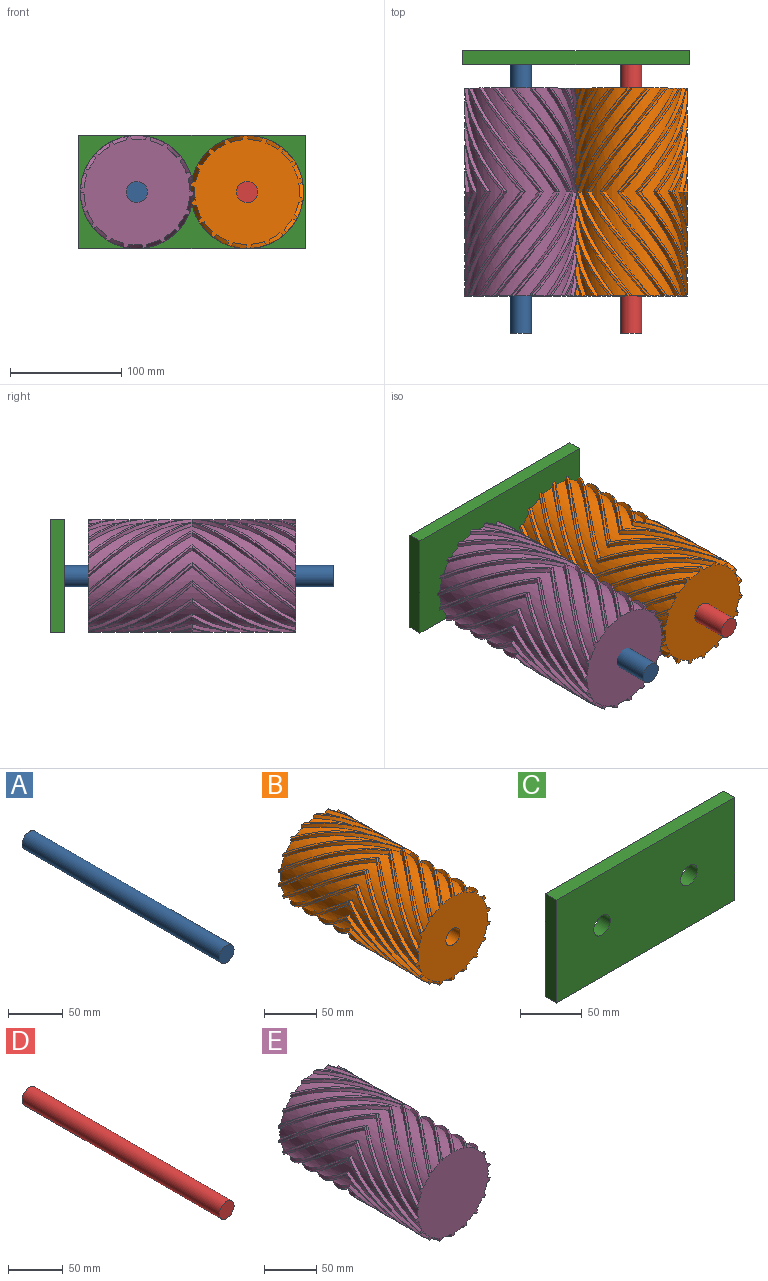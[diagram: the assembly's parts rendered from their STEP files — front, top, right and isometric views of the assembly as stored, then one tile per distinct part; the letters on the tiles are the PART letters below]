
ASSEMBLY  parts=5 mates=4
PART A: 3 faces, bbox 19.1x254x19.1 mm
  f0: cylinder r=9.53mm len=254mm, axis (0,1,0), area 15201.2mm2, adj f1,f2
  f1: plane 19.05x19.05mm, normal (0,-1,0), area 285mm2, adj f0
  f2: plane 19.05x19.05mm, normal (0,1,0), area 285mm2, adj f0
PART B: 129 faces, bbox 102.5x186.9x102.5 mm
  f0: plane 101.65x100.54mm, normal (0,-1,0), area 6946.6mm2, adj f1,f2,f3,f4,f5,f6,f7,f8
  f1: bspline ~93.47x69.89mm, area 471mm2, adj f0,f2,f4,f23
  f2: bspline ~93.47x71.15mm, area 235.9mm2, adj f0,f1,f3,f24
  f3: bspline ~93.47x68.96mm, area 471mm2, adj f0,f2,f16,f25
  f4: cylinder r=47.1mm len=186.94mm, axis (0,1,0), area 2157.7mm2, adj f0,f1,f22,f23,f97,f100
  f5: cylinder r=47.1mm len=186.94mm, axis (0,1,0), area 2157.7mm2, adj f0,f22,f31,f34,f35,f38
  f6: cylinder r=47.1mm len=186.94mm, axis (0,1,0), area 2157.7mm2, adj f0,f22,f37,f40,f41,f44
  f7: cylinder r=47.1mm len=186.94mm, axis (0,1,0), area 2157.7mm2, adj f0,f22,f43,f46,f47,f50
  f8: cylinder r=47.1mm len=186.94mm, axis (0,1,0), area 2157.7mm2, adj f0,f22,f49,f52,f53,f56
  f9: cylinder r=47.1mm len=186.94mm, axis (0,1,0), area 2157.7mm2, adj f0,f22,f55,f58,f59,f62
  f10: cylinder r=47.1mm len=186.94mm, axis (0,1,0), area 2157.7mm2, adj f0,f22,f61,f64,f65,f68
  f11: cylinder r=47.1mm len=186.94mm, axis (0,1,0), area 2157.7mm2, adj f0,f22,f67,f70,f77,f80
  f12: cylinder r=47.1mm len=186.94mm, axis (0,1,0), area 2157.7mm2, adj f0,f22,f73,f76,f89,f92
  f13: cylinder r=47.1mm len=186.94mm, axis (0,1,0), area 2157.7mm2, adj f0,f22,f71,f74,f79,f82
  f14: cylinder r=47.1mm len=186.94mm, axis (0,1,0), area 2157.7mm2, adj f0,f22,f85,f88,f95,f98
  f15: cylinder r=47.1mm len=186.94mm, axis (0,1,0), area 2157.7mm2, adj f0,f22,f83,f86,f91,f94
  f16: cylinder r=47.1mm len=186.94mm, axis (0,1,0), area 2157.7mm2, adj f0,f3,f22,f25,f26,f125
  f17: cylinder r=47.1mm len=186.94mm, axis (0,1,0), area 2157.7mm2, adj f0,f22,f103,f106,f113,f116
  f18: cylinder r=47.1mm len=186.94mm, axis (0,1,0), area 2157.7mm2, adj f0,f22,f29,f32,f109,f112
  f19: cylinder r=47.1mm len=186.94mm, axis (0,1,0), area 2157.7mm2, adj f0,f22,f115,f118,f119,f122
  f20: cylinder r=47.1mm len=186.94mm, axis (0,1,0), area 2157.7mm2, adj f0,f22,f107,f110,f121,f124
  f21: cylinder r=47.1mm len=186.94mm, axis (0,1,0), area 2157.7mm2, adj f0,f22,f28,f101,f104,f127
  f22: plane 101.65x100.54mm, normal (0,1,0), area 6946.6mm2, adj f4,f5,f6,f7,f8,f9,f10,f11
  f23: bspline ~93.47x69.89mm, area 471mm2, adj f1,f4,f22,f24
  f24: bspline ~93.47x71.15mm, area 235.9mm2, adj f2,f22,f23,f25
  f25: bspline ~93.47x68.96mm, area 471mm2, adj f3,f16,f22,f24
  f26: bspline ~93.47x60.41mm, area 471mm2, adj f16,f22,f27,f125
  f27: bspline ~93.47x60.34mm, area 235.9mm2, adj f22,f26,f28,f126
  f28: bspline ~93.47x57.85mm, area 471mm2, adj f21,f22,f27,f127
  f29: bspline ~93.47x53.27mm, area 471mm2, adj f18,f22,f30,f32
  f30: bspline ~93.47x52.25mm, area 235.9mm2, adj f22,f29,f31,f33
  f31: bspline ~93.47x53.27mm, area 471mm2, adj f5,f22,f30,f34
  f32: bspline ~93.47x53.27mm, area 471mm2, adj f0,f18,f29,f33
  f33: bspline ~93.47x52.25mm, area 235.9mm2, adj f0,f30,f32,f34
  f34: bspline ~93.47x53.27mm, area 471mm2, adj f0,f5,f31,f33
  f35: bspline ~93.47x64.39mm, area 471mm2, adj f0,f5,f36,f38
  f36: bspline ~93.47x66.76mm, area 235.9mm2, adj f0,f35,f37,f39
  f37: bspline ~93.47x66.03mm, area 471mm2, adj f0,f6,f36,f40
  f38: bspline ~93.47x64.39mm, area 471mm2, adj f5,f22,f35,f39
  f39: bspline ~93.47x66.76mm, area 235.9mm2, adj f22,f36,f38,f40
  f40: bspline ~93.47x66.03mm, area 471mm2, adj f6,f22,f37,f39
  f41: bspline ~93.47x71.45mm, area 471mm2, adj f0,f6,f42,f44
  f42: bspline ~93.47x73.38mm, area 235.9mm2, adj f0,f41,f43,f45
  f43: bspline ~93.47x71.76mm, area 471mm2, adj f0,f7,f42,f46
  f44: bspline ~93.47x71.45mm, area 471mm2, adj f6,f22,f41,f45
  f45: bspline ~93.47x73.38mm, area 235.9mm2, adj f22,f42,f44,f46
  f46: bspline ~93.47x71.76mm, area 471mm2, adj f7,f22,f43,f45
  f47: bspline ~93.47x69.89mm, area 471mm2, adj f0,f7,f48,f50
  f48: bspline ~93.47x71.15mm, area 235.9mm2, adj f0,f47,f49,f51
  f49: bspline ~93.47x68.96mm, area 471mm2, adj f0,f8,f48,f52
  f50: bspline ~93.47x69.89mm, area 471mm2, adj f7,f22,f47,f51
  f51: bspline ~93.47x71.15mm, area 235.9mm2, adj f22,f48,f50,f52
  f52: bspline ~93.47x68.96mm, area 471mm2, adj f8,f22,f49,f51
  f53: bspline ~93.47x60.41mm, area 471mm2, adj f0,f8,f54,f56
  f54: bspline ~93.47x60.34mm, area 235.9mm2, adj f0,f53,f55,f57
  f55: bspline ~93.47x57.85mm, area 471mm2, adj f0,f9,f54,f58
  f56: bspline ~93.47x60.41mm, area 471mm2, adj f8,f22,f53,f57
  f57: bspline ~93.47x60.34mm, area 235.9mm2, adj f22,f54,f56,f58
  f58: bspline ~93.47x57.85mm, area 471mm2, adj f9,f22,f55,f57
  f59: bspline ~93.47x57.85mm, area 471mm2, adj f0,f9,f60,f62
  f60: bspline ~93.47x60.34mm, area 235.9mm2, adj f0,f59,f61,f63
  f61: bspline ~93.47x60.41mm, area 471mm2, adj f0,f10,f60,f64
  f62: bspline ~93.47x57.85mm, area 471mm2, adj f9,f22,f59,f63
  f63: bspline ~93.47x60.34mm, area 235.9mm2, adj f22,f60,f62,f64
  f64: bspline ~93.47x60.41mm, area 471mm2, adj f10,f22,f61,f63
  f65: bspline ~93.47x68.96mm, area 471mm2, adj f0,f10,f66,f68
  f66: bspline ~93.47x71.15mm, area 235.9mm2, adj f0,f65,f67,f69
  f67: bspline ~93.47x69.89mm, area 471mm2, adj f0,f11,f66,f70
  f68: bspline ~93.47x68.96mm, area 471mm2, adj f10,f22,f65,f69
  f69: bspline ~93.47x71.15mm, area 235.9mm2, adj f22,f66,f68,f70
  f70: bspline ~93.47x69.89mm, area 471mm2, adj f11,f22,f67,f69
  f71: bspline ~93.47x66.03mm, area 471mm2, adj f0,f13,f72,f74
  f72: bspline ~93.47x66.76mm, area 235.9mm2, adj f0,f71,f73,f75
  f73: bspline ~93.47x64.39mm, area 471mm2, adj f0,f12,f72,f76
  f74: bspline ~93.47x66.03mm, area 471mm2, adj f13,f22,f71,f75
  f75: bspline ~93.47x66.76mm, area 235.9mm2, adj f22,f72,f74,f76
  f76: bspline ~93.47x64.39mm, area 471mm2, adj f12,f22,f73,f75
  f77: bspline ~93.47x71.76mm, area 471mm2, adj f0,f11,f78,f80
  f78: bspline ~93.47x73.38mm, area 235.9mm2, adj f0,f77,f79,f81
  f79: bspline ~93.47x71.45mm, area 471mm2, adj f0,f13,f78,f82
  f80: bspline ~93.47x71.76mm, area 471mm2, adj f11,f22,f77,f81
  f81: bspline ~93.47x73.38mm, area 235.9mm2, adj f22,f78,f80,f82
  f82: bspline ~93.47x71.45mm, area 471mm2, adj f13,f22,f79,f81
  f83: bspline ~93.47x64.39mm, area 471mm2, adj f0,f15,f84,f86
  f84: bspline ~93.47x66.76mm, area 235.9mm2, adj f0,f83,f85,f87
  f85: bspline ~93.47x66.03mm, area 471mm2, adj f0,f14,f84,f88
  f86: bspline ~93.47x64.39mm, area 471mm2, adj f15,f22,f83,f87
  f87: bspline ~93.47x66.76mm, area 235.9mm2, adj f22,f84,f86,f88
  f88: bspline ~93.47x66.03mm, area 471mm2, adj f14,f22,f85,f87
  f89: bspline ~93.47x53.27mm, area 471mm2, adj f0,f12,f90,f92
  f90: bspline ~93.47x52.25mm, area 235.9mm2, adj f0,f89,f91,f93
  f91: bspline ~93.47x53.27mm, area 471mm2, adj f0,f15,f90,f94
  f92: bspline ~93.47x53.27mm, area 471mm2, adj f12,f22,f89,f93
  f93: bspline ~93.47x52.25mm, area 235.9mm2, adj f22,f90,f92,f94
  f94: bspline ~93.47x53.27mm, area 471mm2, adj f15,f22,f91,f93
  f95: bspline ~93.47x71.45mm, area 471mm2, adj f0,f14,f96,f98
  f96: bspline ~93.47x73.38mm, area 235.9mm2, adj f0,f95,f97,f99
  f97: bspline ~93.47x71.76mm, area 471mm2, adj f0,f4,f96,f100
  f98: bspline ~93.47x71.45mm, area 471mm2, adj f14,f22,f95,f99
  f99: bspline ~93.47x73.38mm, area 235.9mm2, adj f22,f96,f98,f100
  f100: bspline ~93.47x71.76mm, area 471mm2, adj f4,f22,f97,f99
  f101: bspline ~93.47x57.85mm, area 471mm2, adj f21,f22,f102,f104
  f102: bspline ~93.47x60.34mm, area 235.9mm2, adj f22,f101,f103,f105
  f103: bspline ~93.47x60.41mm, area 471mm2, adj f17,f22,f102,f106
  f104: bspline ~93.47x57.85mm, area 471mm2, adj f0,f21,f101,f105
  f105: bspline ~93.47x60.34mm, area 235.9mm2, adj f0,f102,f104,f106
  f106: bspline ~93.47x60.41mm, area 471mm2, adj f0,f17,f103,f105
  f107: bspline ~93.47x66.03mm, area 471mm2, adj f20,f22,f108,f110
  f108: bspline ~93.47x66.76mm, area 235.9mm2, adj f22,f107,f109,f111
  f109: bspline ~93.47x64.39mm, area 471mm2, adj f18,f22,f108,f112
  f110: bspline ~93.47x66.03mm, area 471mm2, adj f0,f20,f107,f111
  f111: bspline ~93.47x66.76mm, area 235.9mm2, adj f0,f108,f110,f112
  f112: bspline ~93.47x64.39mm, area 471mm2, adj f0,f18,f109,f111
  f113: bspline ~93.47x68.96mm, area 471mm2, adj f17,f22,f114,f116
  f114: bspline ~93.47x71.15mm, area 235.9mm2, adj f22,f113,f115,f117
  f115: bspline ~93.47x69.89mm, area 471mm2, adj f19,f22,f114,f118
  f116: bspline ~93.47x68.96mm, area 471mm2, adj f0,f17,f113,f117
  f117: bspline ~93.47x71.15mm, area 235.9mm2, adj f0,f114,f116,f118
  f118: bspline ~93.47x69.89mm, area 471mm2, adj f0,f19,f115,f117
  f119: bspline ~93.47x71.76mm, area 471mm2, adj f19,f22,f120,f122
  f120: bspline ~93.47x73.38mm, area 235.9mm2, adj f22,f119,f121,f123
  f121: bspline ~93.47x71.45mm, area 471mm2, adj f20,f22,f120,f124
  f122: bspline ~93.47x71.76mm, area 471mm2, adj f0,f19,f119,f123
  f123: bspline ~93.47x73.38mm, area 235.9mm2, adj f0,f120,f122,f124
  f124: bspline ~93.47x71.45mm, area 471mm2, adj f0,f20,f121,f123
  f125: bspline ~93.47x60.41mm, area 471mm2, adj f0,f16,f26,f126
  f126: bspline ~93.47x60.34mm, area 235.9mm2, adj f0,f27,f125,f127
  f127: bspline ~93.47x57.85mm, area 471mm2, adj f0,f21,f28,f126
  f128: cylinder r=9.53mm len=186.94mm, axis (0,1,0), area 11188.1mm2, adj f0,f22
PART C: 8 faces, bbox 203.2x12.7x101.6 mm
  f0: plane 101.6x12.7mm, normal (-1,0,0), area 1290.3mm2, adj f1,f4,f6,f7
  f1: plane 203.2x12.7mm, normal (0,0,-1), area 2580.6mm2, adj f0,f2,f6,f7
  f2: plane 101.6x12.7mm, normal (1,0,0), area 1290.3mm2, adj f1,f4,f6,f7
  f3: cylinder r=9.53mm len=19.05mm, axis (0,-1,0), area 760.1mm2, adj f6,f7
  f4: plane 203.2x12.7mm, normal (0,0,1), area 2580.6mm2, adj f0,f2,f6,f7
  f5: cylinder r=9.53mm len=19.05mm, axis (0,-1,0), area 760.1mm2, adj f6,f7
  f6: plane 203.2x101.6mm, normal (0,1,0), area 20075.1mm2, adj f0,f1,f2,f3,f4,f5
  f7: plane 203.2x101.6mm, normal (0,-1,0), area 20075.1mm2, adj f0,f1,f2,f3,f4,f5
PART D: 3 faces, bbox 19.1x254x19.1 mm
  f0: cylinder r=9.53mm len=254mm, axis (0,1,0), area 15201.2mm2, adj f1,f2
  f1: plane 19.05x19.05mm, normal (0,-1,0), area 285mm2, adj f0
  f2: plane 19.05x19.05mm, normal (0,1,0), area 285mm2, adj f0
PART E: 128 faces, bbox 102.5x186.9x102.5 mm
  f0: plane 101.65x100.54mm, normal (0,-1,0), area 7343.5mm2, adj f1,f2,f3,f4,f5,f6,f7,f8
  f1: bspline ~93.47x69.89mm, area 406.7mm2, adj f0,f2,f4,f23
  f2: bspline ~93.47x71.15mm, area 235.9mm2, adj f0,f1,f3,f24
  f3: bspline ~93.47x68.96mm, area 406.7mm2, adj f0,f2,f16,f25
  f4: cylinder r=47.62mm len=186.94mm, axis (0,1,0), area 2227.2mm2, adj f0,f1,f22,f23,f97,f100
  f5: cylinder r=47.62mm len=186.94mm, axis (0,1,0), area 2227.2mm2, adj f0,f22,f31,f34,f35,f38
  f6: cylinder r=47.62mm len=186.94mm, axis (0,1,0), area 2227.2mm2, adj f0,f22,f37,f40,f41,f44
  f7: cylinder r=47.62mm len=186.94mm, axis (0,1,0), area 2227.2mm2, adj f0,f22,f43,f46,f47,f50
  f8: cylinder r=47.62mm len=186.94mm, axis (0,1,0), area 2227.2mm2, adj f0,f22,f49,f52,f53,f56
  f9: cylinder r=47.62mm len=186.94mm, axis (0,1,0), area 2227.2mm2, adj f0,f22,f55,f58,f59,f62
  f10: cylinder r=47.62mm len=186.94mm, axis (0,1,0), area 2227.2mm2, adj f0,f22,f61,f64,f65,f68
  f11: cylinder r=47.62mm len=186.94mm, axis (0,1,0), area 2227.2mm2, adj f0,f22,f67,f70,f77,f80
  f12: cylinder r=47.62mm len=186.94mm, axis (0,1,0), area 2227.2mm2, adj f0,f22,f73,f76,f89,f92
  f13: cylinder r=47.62mm len=186.94mm, axis (0,1,0), area 2227.2mm2, adj f0,f22,f71,f74,f79,f82
  f14: cylinder r=47.62mm len=186.94mm, axis (0,1,0), area 2227.2mm2, adj f0,f22,f85,f88,f95,f98
  f15: cylinder r=47.62mm len=186.94mm, axis (0,1,0), area 2227.2mm2, adj f0,f22,f83,f86,f91,f94
  f16: cylinder r=47.62mm len=186.94mm, axis (0,1,0), area 2227.2mm2, adj f0,f3,f22,f25,f26,f125
  f17: cylinder r=47.62mm len=186.94mm, axis (0,1,0), area 2227.2mm2, adj f0,f22,f103,f106,f113,f116
  f18: cylinder r=47.62mm len=186.94mm, axis (0,1,0), area 2227.2mm2, adj f0,f22,f29,f32,f109,f112
  f19: cylinder r=47.62mm len=186.94mm, axis (0,1,0), area 2227.2mm2, adj f0,f22,f115,f118,f119,f122
  f20: cylinder r=47.62mm len=186.94mm, axis (0,1,0), area 2227.2mm2, adj f0,f22,f107,f110,f121,f124
  f21: cylinder r=47.62mm len=186.94mm, axis (0,1,0), area 2227.2mm2, adj f0,f22,f28,f101,f104,f127
  f22: plane 101.65x100.54mm, normal (0,1,0), area 7343.5mm2, adj f4,f5,f6,f7,f8,f9,f10,f11
  f23: bspline ~93.47x69.89mm, area 406.7mm2, adj f1,f4,f22,f24
  f24: bspline ~93.47x71.15mm, area 235.9mm2, adj f2,f22,f23,f25
  f25: bspline ~93.47x68.96mm, area 406.7mm2, adj f3,f16,f22,f24
  f26: bspline ~93.47x60.41mm, area 406.7mm2, adj f16,f22,f27,f125
  f27: bspline ~93.47x60.34mm, area 235.9mm2, adj f22,f26,f28,f126
  f28: bspline ~93.47x57.85mm, area 406.7mm2, adj f21,f22,f27,f127
  f29: bspline ~93.47x53.18mm, area 406.7mm2, adj f18,f22,f30,f32
  f30: bspline ~93.47x52.25mm, area 235.9mm2, adj f22,f29,f31,f33
  f31: bspline ~93.47x53.18mm, area 406.7mm2, adj f5,f22,f30,f34
  f32: bspline ~93.47x53.18mm, area 406.7mm2, adj f0,f18,f29,f33
  f33: bspline ~93.47x52.25mm, area 235.9mm2, adj f0,f30,f32,f34
  f34: bspline ~93.47x53.18mm, area 406.7mm2, adj f0,f5,f31,f33
  f35: bspline ~93.47x64.39mm, area 406.7mm2, adj f0,f5,f36,f38
  f36: bspline ~93.47x66.76mm, area 235.9mm2, adj f0,f35,f37,f39
  f37: bspline ~93.47x66.02mm, area 406.7mm2, adj f0,f6,f36,f40
  f38: bspline ~93.47x64.39mm, area 406.7mm2, adj f5,f22,f35,f39
  f39: bspline ~93.47x66.76mm, area 235.9mm2, adj f22,f36,f38,f40
  f40: bspline ~93.47x66.02mm, area 406.7mm2, adj f6,f22,f37,f39
  f41: bspline ~93.47x71.45mm, area 406.7mm2, adj f0,f6,f42,f44
  f42: bspline ~93.47x73.38mm, area 235.9mm2, adj f0,f41,f43,f45
  f43: bspline ~93.47x71.76mm, area 406.7mm2, adj f0,f7,f42,f46
  f44: bspline ~93.47x71.45mm, area 406.7mm2, adj f6,f22,f41,f45
  f45: bspline ~93.47x73.38mm, area 235.9mm2, adj f22,f42,f44,f46
  f46: bspline ~93.47x71.76mm, area 406.7mm2, adj f7,f22,f43,f45
  f47: bspline ~93.47x69.89mm, area 406.7mm2, adj f0,f7,f48,f50
  f48: bspline ~93.47x71.15mm, area 235.9mm2, adj f0,f47,f49,f51
  f49: bspline ~93.47x68.96mm, area 406.7mm2, adj f0,f8,f48,f52
  f50: bspline ~93.47x69.89mm, area 406.7mm2, adj f7,f22,f47,f51
  f51: bspline ~93.47x71.15mm, area 235.9mm2, adj f22,f48,f50,f52
  f52: bspline ~93.47x68.96mm, area 406.7mm2, adj f8,f22,f49,f51
  f53: bspline ~93.47x60.41mm, area 406.7mm2, adj f0,f8,f54,f56
  f54: bspline ~93.47x60.34mm, area 235.9mm2, adj f0,f53,f55,f57
  f55: bspline ~93.47x57.85mm, area 406.7mm2, adj f0,f9,f54,f58
  f56: bspline ~93.47x60.41mm, area 406.7mm2, adj f8,f22,f53,f57
  f57: bspline ~93.47x60.34mm, area 235.9mm2, adj f22,f54,f56,f58
  f58: bspline ~93.47x57.85mm, area 406.7mm2, adj f9,f22,f55,f57
  f59: bspline ~93.47x57.85mm, area 406.7mm2, adj f0,f9,f60,f62
  f60: bspline ~93.47x60.34mm, area 235.9mm2, adj f0,f59,f61,f63
  f61: bspline ~93.47x60.41mm, area 406.7mm2, adj f0,f10,f60,f64
  f62: bspline ~93.47x57.85mm, area 406.7mm2, adj f9,f22,f59,f63
  f63: bspline ~93.47x60.34mm, area 235.9mm2, adj f22,f60,f62,f64
  f64: bspline ~93.47x60.41mm, area 406.7mm2, adj f10,f22,f61,f63
  f65: bspline ~93.47x68.96mm, area 406.7mm2, adj f0,f10,f66,f68
  f66: bspline ~93.47x71.15mm, area 235.9mm2, adj f0,f65,f67,f69
  f67: bspline ~93.47x69.89mm, area 406.7mm2, adj f0,f11,f66,f70
  f68: bspline ~93.47x68.96mm, area 406.7mm2, adj f10,f22,f65,f69
  f69: bspline ~93.47x71.15mm, area 235.9mm2, adj f22,f66,f68,f70
  f70: bspline ~93.47x69.89mm, area 406.7mm2, adj f11,f22,f67,f69
  f71: bspline ~93.47x66.02mm, area 406.7mm2, adj f0,f13,f72,f74
  f72: bspline ~93.47x66.76mm, area 235.9mm2, adj f0,f71,f73,f75
  f73: bspline ~93.47x64.39mm, area 406.7mm2, adj f0,f12,f72,f76
  f74: bspline ~93.47x66.02mm, area 406.7mm2, adj f13,f22,f71,f75
  f75: bspline ~93.47x66.76mm, area 235.9mm2, adj f22,f72,f74,f76
  f76: bspline ~93.47x64.39mm, area 406.7mm2, adj f12,f22,f73,f75
  f77: bspline ~93.47x71.76mm, area 406.7mm2, adj f0,f11,f78,f80
  f78: bspline ~93.47x73.38mm, area 235.9mm2, adj f0,f77,f79,f81
  f79: bspline ~93.47x71.45mm, area 406.7mm2, adj f0,f13,f78,f82
  f80: bspline ~93.47x71.76mm, area 406.7mm2, adj f11,f22,f77,f81
  f81: bspline ~93.47x73.38mm, area 235.9mm2, adj f22,f78,f80,f82
  f82: bspline ~93.47x71.45mm, area 406.7mm2, adj f13,f22,f79,f81
  f83: bspline ~93.47x64.39mm, area 406.7mm2, adj f0,f15,f84,f86
  f84: bspline ~93.47x66.76mm, area 235.9mm2, adj f0,f83,f85,f87
  f85: bspline ~93.47x66.02mm, area 406.7mm2, adj f0,f14,f84,f88
  f86: bspline ~93.47x64.39mm, area 406.7mm2, adj f15,f22,f83,f87
  f87: bspline ~93.47x66.76mm, area 235.9mm2, adj f22,f84,f86,f88
  f88: bspline ~93.47x66.02mm, area 406.7mm2, adj f14,f22,f85,f87
  f89: bspline ~93.47x53.18mm, area 406.7mm2, adj f0,f12,f90,f92
  f90: bspline ~93.47x52.25mm, area 235.9mm2, adj f0,f89,f91,f93
  f91: bspline ~93.47x53.18mm, area 406.7mm2, adj f0,f15,f90,f94
  f92: bspline ~93.47x53.18mm, area 406.7mm2, adj f12,f22,f89,f93
  f93: bspline ~93.47x52.25mm, area 235.9mm2, adj f22,f90,f92,f94
  f94: bspline ~93.47x53.18mm, area 406.7mm2, adj f15,f22,f91,f93
  f95: bspline ~93.47x71.45mm, area 406.7mm2, adj f0,f14,f96,f98
  f96: bspline ~93.47x73.38mm, area 235.9mm2, adj f0,f95,f97,f99
  f97: bspline ~93.47x71.76mm, area 406.7mm2, adj f0,f4,f96,f100
  f98: bspline ~93.47x71.45mm, area 406.7mm2, adj f14,f22,f95,f99
  f99: bspline ~93.47x73.38mm, area 235.9mm2, adj f22,f96,f98,f100
  f100: bspline ~93.47x71.76mm, area 406.7mm2, adj f4,f22,f97,f99
  f101: bspline ~93.47x57.85mm, area 406.7mm2, adj f21,f22,f102,f104
  f102: bspline ~93.47x60.34mm, area 235.9mm2, adj f22,f101,f103,f105
  f103: bspline ~93.47x60.41mm, area 406.7mm2, adj f17,f22,f102,f106
  f104: bspline ~93.47x57.85mm, area 406.7mm2, adj f0,f21,f101,f105
  f105: bspline ~93.47x60.34mm, area 235.9mm2, adj f0,f102,f104,f106
  f106: bspline ~93.47x60.41mm, area 406.7mm2, adj f0,f17,f103,f105
  f107: bspline ~93.47x66.02mm, area 406.7mm2, adj f20,f22,f108,f110
  f108: bspline ~93.47x66.76mm, area 235.9mm2, adj f22,f107,f109,f111
  f109: bspline ~93.47x64.39mm, area 406.7mm2, adj f18,f22,f108,f112
  f110: bspline ~93.47x66.02mm, area 406.7mm2, adj f0,f20,f107,f111
  f111: bspline ~93.47x66.76mm, area 235.9mm2, adj f0,f108,f110,f112
  f112: bspline ~93.47x64.39mm, area 406.7mm2, adj f0,f18,f109,f111
  f113: bspline ~93.47x68.96mm, area 406.7mm2, adj f17,f22,f114,f116
  f114: bspline ~93.47x71.15mm, area 235.9mm2, adj f22,f113,f115,f117
  f115: bspline ~93.47x69.89mm, area 406.7mm2, adj f19,f22,f114,f118
  f116: bspline ~93.47x68.96mm, area 406.7mm2, adj f0,f17,f113,f117
  f117: bspline ~93.47x71.15mm, area 235.9mm2, adj f0,f114,f116,f118
  f118: bspline ~93.47x69.89mm, area 406.7mm2, adj f0,f19,f115,f117
  f119: bspline ~93.47x71.76mm, area 406.7mm2, adj f19,f22,f120,f122
  f120: bspline ~93.47x73.38mm, area 235.9mm2, adj f22,f119,f121,f123
  f121: bspline ~93.47x71.45mm, area 406.7mm2, adj f20,f22,f120,f124
  f122: bspline ~93.47x71.76mm, area 406.7mm2, adj f0,f19,f119,f123
  f123: bspline ~93.47x73.38mm, area 235.9mm2, adj f0,f120,f122,f124
  f124: bspline ~93.47x71.45mm, area 406.7mm2, adj f0,f20,f121,f123
  f125: bspline ~93.47x60.41mm, area 406.7mm2, adj f0,f16,f26,f126
  f126: bspline ~93.47x60.34mm, area 235.9mm2, adj f0,f27,f125,f127
  f127: bspline ~93.47x57.85mm, area 406.7mm2, adj f0,f21,f28,f126
PLACE A t=(22.2,238.7,174.31)mm
PLACE B rot(axis=(0.51,0,-0.86),180deg) t=(71.73,111.7,174.31)mm
PLACE C t=(22.2,226,174.31)mm fixed
PLACE D t=(22.2,238.7,174.31)mm
PLACE E rot(axis=(0,-1,0),28.1deg) t=(-27.33,111.7,174.31)mm
MATE revolute B.f4 <-> D.f0  axis (0,-1,0) through (71.73,111.7,174.31)mm
MATE fastened A.f0 <-> C.f3  axis (0,1,0) through (-27.33,238.7,174.31)mm
MATE revolute E.f4 <-> A.f0  axis (0,1,0) through (-27.33,111.7,174.31)mm
MATE fastened D.f0 <-> C.f5  axis (0,1,0) through (71.73,238.7,174.31)mm
